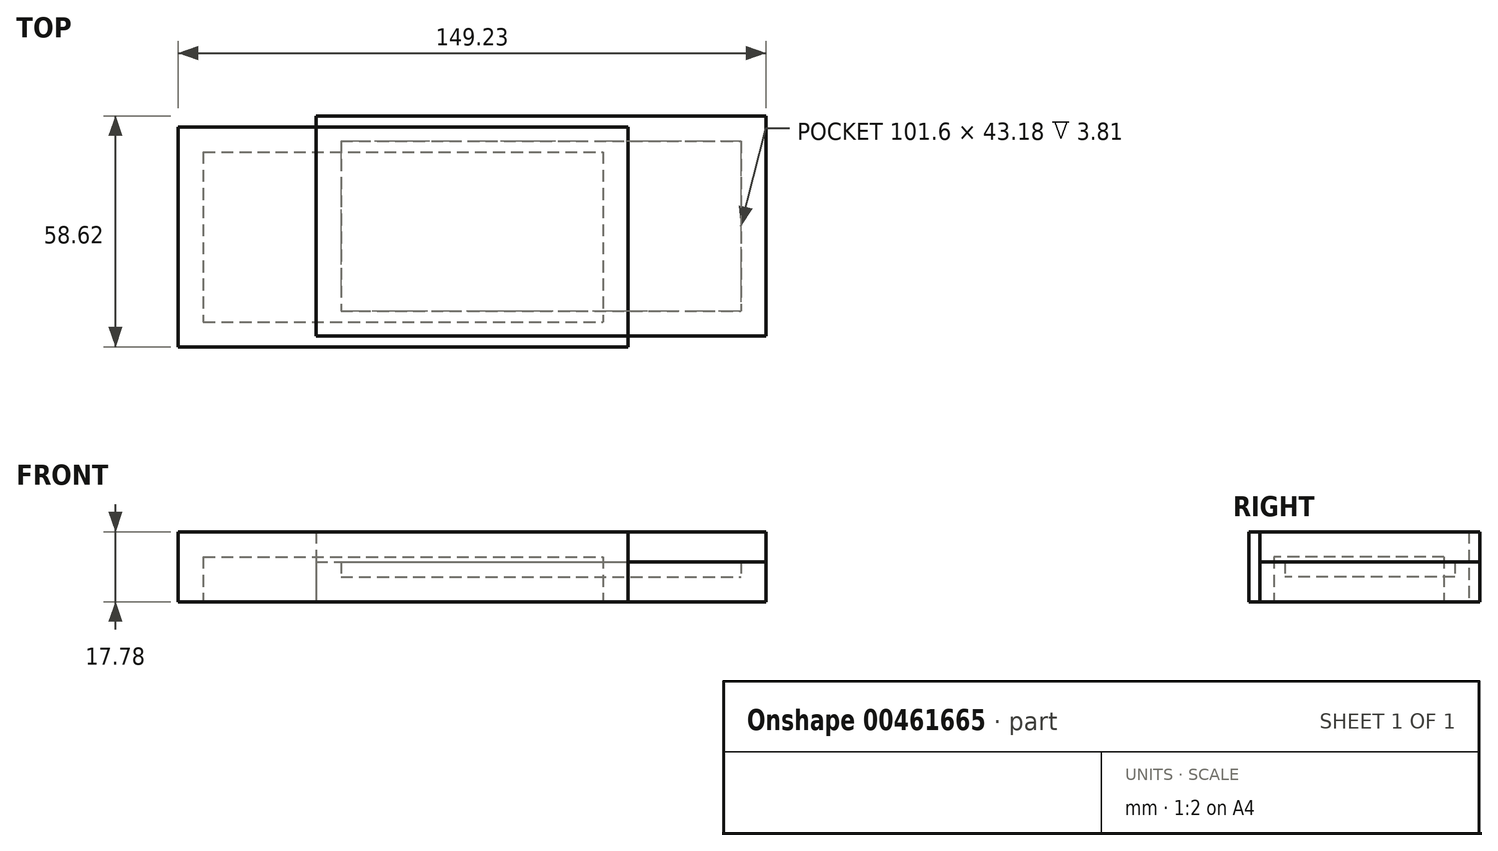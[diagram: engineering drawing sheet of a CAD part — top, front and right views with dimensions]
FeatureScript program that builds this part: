
annotation { "Feature Type Name" : "Feature", "Feature Type Description" : "" }
export const myFeature = defineFeature(function(context is Context, id is Id, definition is map)
    precondition{}
    {
        {
            var Q0;
            Q0=qCreatedBy(makeId("Top.planeOp"),FACE);
            var sketch = newSketch(context, id + "F0", { "sketchPlane" : qUnion([Q0])});
            skLineSegment(sketch, "E0.bottom", {"start": v(-56.58, 13.77) * mm, "end": v(57.72, 13.77) * mm});
            skLineSegment(sketch, "E0.top", {"start": v(-56.58, -42.11) * mm, "end": v(57.72, -42.11) * mm});
            skLineSegment(sketch, "E0.left", {"start": v(-56.58, 13.77) * mm, "end": v(-56.58, -42.11) * mm});
            skLineSegment(sketch, "E0.right", {"start": v(57.72, 13.77) * mm, "end": v(57.72, -42.11) * mm});
            skSolve(sketch);
        }
        {
            var Q0;
            Q0 = qSketchRegion(id + "F0", true);
            extrude(context, id + "F1", {"entities" : qUnion([Q0]), "depth" : 10.16 * mm, "offsetDistance" : 25.4 * mm});
        }
        {
            var Q0;
            Q0=qCreatedBy(makeId("Top.planeOp"),FACE);
            var sketch = newSketch(context, id + "F2", { "sketchPlane" : qUnion([Q0])});
            skLineSegment(sketch, "E1.bottom", {"start": v(-91.51, 11.03) * mm, "end": v(22.79, 11.03) * mm});
            skLineSegment(sketch, "E1.top", {"start": v(-91.51, -44.85) * mm, "end": v(22.79, -44.85) * mm});
            skLineSegment(sketch, "E1.left", {"start": v(-91.51, 11.03) * mm, "end": v(-91.51, -44.85) * mm});
            skLineSegment(sketch, "E1.right", {"start": v(22.79, 11.03) * mm, "end": v(22.79, -44.85) * mm});
            skSolve(sketch);
        }
        {
            var Q0;
            Q0 = qSketchRegion(id + "F2", true);
            var Q1;
            Q1 = qSketchRegion(id + "F0", true);
            extrude(context, id + "F3", {"entities" : qUnion([Q0, Q1]), "depth" : 17.78 * mm});
        }
        {
            var Q0;
            Q0=makeQuery(id+"F3.opExtrude","CAP_FACE",FACE,{"disambiguationData":[OSD([sQuery(id+"F2.wireOp",EDGE,"E1.bottom"),sQuery(id+"F2.wireOp",EDGE,"E1.top"),sQuery(id+"F2.wireOp",EDGE,"E1.left"),sQuery(id+"F2.wireOp",EDGE,"E1.right")])],"isStart":true});
            shell(context, id + "F4", {"entities" : qUnion([Q0]), "thickness" : 6.35 * mm});
        }
        {
            var Q0;
            Q0=makeQuery(id+"F1.opExtrude","CAP_FACE",FACE,{"disambiguationData":[OSD([sQuery(id+"F0.wireOp",EDGE,"E0.bottom"),sQuery(id+"F0.wireOp",EDGE,"E0.top"),sQuery(id+"F0.wireOp",EDGE,"E0.left"),sQuery(id+"F0.wireOp",EDGE,"E0.right")])],"isStart":false});
            shell(context, id + "F5", {"entities" : qUnion([Q0]), "thickness" : 6.35 * mm});
        }
    });
